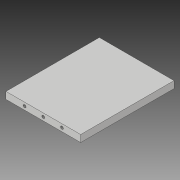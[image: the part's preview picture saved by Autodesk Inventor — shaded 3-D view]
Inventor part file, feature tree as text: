
AUTODESK INVENTOR PART (.ipt)
format: ipt  version: 2019 (Build 230136000, 136)  size: 94,720 bytes
history: native  units: mm
features: sketch x3, hole x2, extrude x1
ambient origin geometry x8: Origin, YZ Plane, XZ Plane, XY Plane, X Axis, Y Axis, Z Axis, Center Point
bodies: Solid1 (feature_tree)
feature tree (6):
  extrude  "Extrusion1"  Depth=135.0mm
  hole  "Hole1"  [1 undecoded]
  hole  "Hole2"  [1 undecoded]
  sketch  "Sketch1"  dims[d0=108.0mm d1=135.0mm]
  sketch  "Sketch2"  dims[d2=10.0mm d3=0.0mm d4=54.0mm]
  sketch  "Sketch3"  dims[d5=4.134mm d6=10.0mm d7=4.0mm d8=2.0mm d9=90.0deg d10=14.2mm d11=20.594885mm d12=4.134mm d13=10.0mm d14=4.0mm d15=2.0mm d16=90.0deg d17=14.2mm d18=20.594885mm]
note: 2 required parameter values undecoded (feature->parameter linkage not recoverable at this tier; creation-order binding heuristic only, values carry confidence <= 0.55)
